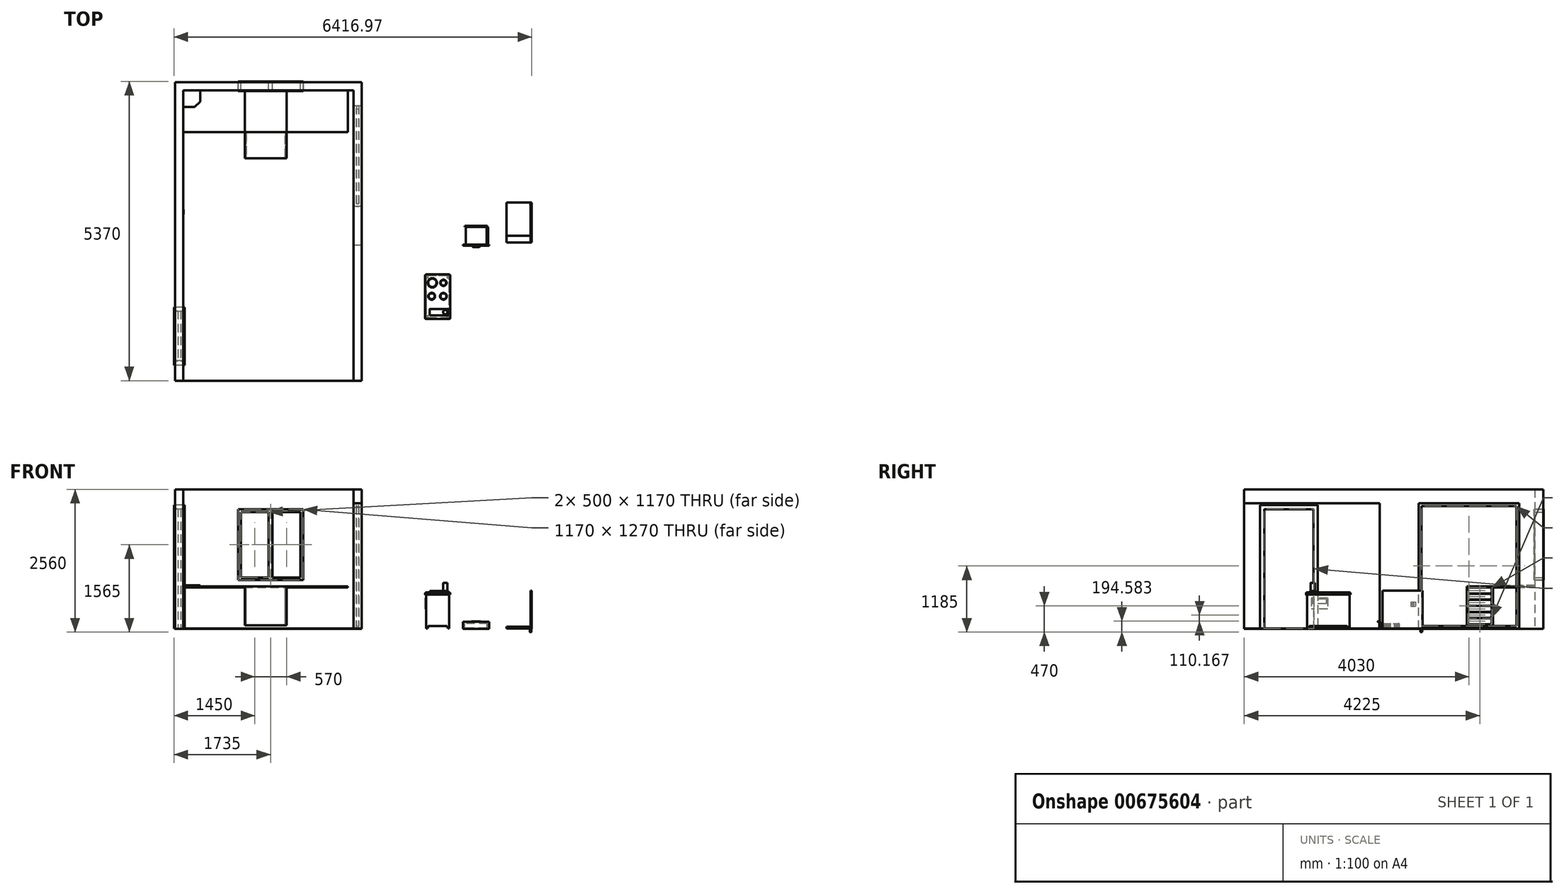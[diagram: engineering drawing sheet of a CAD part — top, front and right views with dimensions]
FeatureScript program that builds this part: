
annotation { "Feature Type Name" : "Feature", "Feature Type Description" : "" }
export const myFeature = defineFeature(function(context is Context, id is Id, definition is map)
    precondition{}
    {
        {
            var Q0;
            Q0=qCreatedBy(makeId("Top.planeOp"),FACE);
            var sketch = newSketch(context, id + "F0", { "sketchPlane" : qUnion([Q0])});
            skLineSegment(sketch, "E0.bottom", {"start": v(-128.32, 3885.41) * mm, "end": v(2921.68, 3885.41) * mm});
            skLineSegment(sketch, "E0.top", {"start": v(-128.32, -74.59) * mm, "end": v(2921.68, -74.59) * mm});
            skLineSegment(sketch, "E0.left", {"start": v(-128.32, 3885.41) * mm, "end": v(-128.32, -74.59) * mm});
            skLineSegment(sketch, "E0.right", {"start": v(2921.68, 3885.41) * mm, "end": v(2921.68, -74.59) * mm});
            skSolve(sketch);
        }
        {
            var Q0;
            Q0=makeQuery(id+"F0.imprint","IMPRINT",FACE,{"disambiguationData":[TD([[makeQuery(id+"F0.imprint","IMPRINT",EDGE,{"derivedFrom":sQuery(id+"F0.wireOp",EDGE,"E0.bottom")}),-1.0]])]});
            var sketch = newSketch(context, id + "F1", { "sketchPlane" : qUnion([Q0])});
            skLineSegment(sketch, "E1.bottom", {"start": v(-278.32, -74.59) * mm, "end": v(-128.32, -74.59) * mm});
            skLineSegment(sketch, "E1.top", {"start": v(-278.32, 4035.41) * mm, "end": v(-128.32, 4035.41) * mm});
            skLineSegment(sketch, "E1.left", {"start": v(-278.32, -74.59) * mm, "end": v(-278.32, 4035.41) * mm});
            skLineSegment(sketch, "E1.right", {"start": v(-128.32, -74.59) * mm, "end": v(-128.32, 3885.41) * mm});
            skLineSegment(sketch, "E2.bottom", {"start": v(-128.32, 4035.41) * mm, "end": v(3071.68, 4035.41) * mm});
            skLineSegment(sketch, "E2.top", {"start": v(-128.32, 3885.41) * mm, "end": v(2921.68, 3885.41) * mm});
            skLineSegment(sketch, "E2.right", {"start": v(3071.68, 4035.41) * mm, "end": v(3071.68, 3885.41) * mm});
            skLineSegment(sketch, "E3.top", {"start": v(3071.68, 3605.41) * mm, "end": v(2921.68, 3605.41) * mm});
            skLineSegment(sketch, "E3.left", {"start": v(3071.68, 3885.41) * mm, "end": v(3071.68, 3605.41) * mm});
            skLineSegment(sketch, "E3.right", {"start": v(2921.68, 3885.41) * mm, "end": v(2921.68, 3605.41) * mm});
            skSolve(sketch);
        }
        {
            var Q0;
            Q0 = qSketchRegion(id + "F1", true);
            extrude(context, id + "F2", {"entities" : qUnion([Q0]), "depth" : 2500 * mm, "offsetDistance" : 25 * mm});
        }
        {
            var Q0;
            Q0=makeQuery(id+"F2.opExtrude","CAP_FACE",FACE,{"disambiguationData":[OSD([sQuery(id+"F1.wireOp",EDGE,"E1.bottom"),sQuery(id+"F1.wireOp",EDGE,"E1.top"),sQuery(id+"F1.wireOp",EDGE,"E1.left"),sQuery(id+"F1.wireOp",EDGE,"E1.right"),sQuery(id+"F1.wireOp",EDGE,"E2.bottom"),sQuery(id+"F1.wireOp",EDGE,"E2.top"),sQuery(id+"F1.wireOp",EDGE,"E2.right"),sQuery(id+"F1.wireOp",EDGE,"E3.top"),sQuery(id+"F1.wireOp",EDGE,"E3.left"),sQuery(id+"F1.wireOp",EDGE,"E3.right")])],"isStart":true});
            var sketch = newSketch(context, id + "F3", { "sketchPlane" : qUnion([Q0])});
            skLineSegment(sketch, "E4.bottom", {"start": v(-278.32, -4035.41) * mm, "end": v(3071.68, -4035.41) * mm});
            skLineSegment(sketch, "E4.top", {"start": v(-278.32, 1324.59) * mm, "end": v(3071.68, 1324.59) * mm});
            skLineSegment(sketch, "E4.left", {"start": v(-278.32, -4035.41) * mm, "end": v(-278.32, 1324.59) * mm});
            skLineSegment(sketch, "E4.right", {"start": v(3071.68, -4035.41) * mm, "end": v(3071.68, 1324.59) * mm});
            skSolve(sketch);
        }
        {
            var Q0;
            Q0 = qSketchRegion(id + "F3", true);
            extrude(context, id + "F4", {"entities" : qUnion([Q0]), "depth" : 5 * mm, "offsetDistance" : 25 * mm});
        }
        {
            var Q0;
            Q0=makeQuery(id+"F2.opExtrude","SWEPT_FACE",FACE,{"disambiguationData":[OSD([sQuery(id+"F1.wireOp",EDGE,"E1.left")])]});
            var sketch = newSketch(context, id + "F5", { "sketchPlane" : qUnion([Q0])});
            skLineSegment(sketch, "E5.bottom", {"start": v(74.59, 0) * mm, "end": v(974.59, 0) * mm});
            skLineSegment(sketch, "E5.top", {"start": v(74.59, 2150) * mm, "end": v(974.59, 2150) * mm});
            skLineSegment(sketch, "E5.left", {"start": v(74.59, 0) * mm, "end": v(74.59, 2150) * mm});
            skLineSegment(sketch, "E5.right", {"start": v(974.59, 0) * mm, "end": v(974.59, 2150) * mm});
            skSolve(sketch);
        }
        {
            var Q0;
            Q0 = qSketchRegion(id + "F5", true);
            extrude(context, id + "F6", {"entities" : qUnion([Q0]), "oppositeDirection" : true, "depth" : 100 * mm, "offsetDistance" : 25 * mm, "hasSecondDirection" : true, "secondDirectionOppositeDirection" : true, "secondDirectionDepth" : 50 * mm});
        }
        {
            var Q0;
            Q0=makeQuery(id+"F2.opExtrude","SWEPT_FACE",FACE,{"disambiguationData":[OSD([sQuery(id+"F1.wireOp",EDGE,"E1.left")])]});
            var sketch = newSketch(context, id + "F7", { "sketchPlane" : qUnion([Q0])});
            skLineSegment(sketch, "E6.bottom", {"start": v(74.59, 2150) * mm, "end": v(974.59, 2150) * mm});
            skLineSegment(sketch, "E6.top", {"start": v(74.59, 2500) * mm, "end": v(974.59, 2500) * mm});
            skLineSegment(sketch, "E6.left", {"start": v(74.59, 2150) * mm, "end": v(74.59, 2500) * mm});
            skLineSegment(sketch, "E6.right", {"start": v(974.59, 2150) * mm, "end": v(974.59, 2500) * mm});
            skLineSegment(sketch, "E7.bottom", {"start": v(974.59, 2500) * mm, "end": v(1324.59, 2500) * mm});
            skLineSegment(sketch, "E7.top", {"start": v(974.59, 0) * mm, "end": v(1324.59, 0) * mm});
            skLineSegment(sketch, "E7.left", {"start": v(974.59, 2500) * mm, "end": v(974.59, 0) * mm});
            skLineSegment(sketch, "E7.right", {"start": v(1324.59, 2500) * mm, "end": v(1324.59, 0) * mm});
            skSolve(sketch);
        }
        {
            var Q0;
            Q0 = qSketchRegion(id + "F7", true);
            var Q1;
            Q1=makeQuery(id+"F2.opExtrude","SWEPT_FACE",FACE,{"disambiguationData":[OSD([sQuery(id+"F1.wireOp",EDGE,"E1.right")])]});
            extrude(context, id + "F8", {"entities" : qUnion([Q0]), "operationType" : NewBodyOperationType.ADD, "endBound" : BoundingType.UP_TO_SURFACE, "oppositeDirection" : true, "depth" : 25 * mm, "endBoundEntityFace" : qUnion([Q1]), "offsetDistance" : 25 * mm});
        }
        {
            var Q0;
            {var subQ0=sQuery(id+"F1.wireOp",EDGE,"E1.right");Q0=makeQuery(id+"F8.boolean.opBoolean","MERGE",FACE,{"derivedFrom":[makeQuery(id+"F2.opExtrude","SWEPT_FACE",FACE,{"disambiguationData":[OSD([subQ0])]}),makeQuery(id+"F8.opExtrude","CAP_FACE",FACE,{"disambiguationData":[OSD([subQ0])],"isStart":false})]});}
            var sketch = newSketch(context, id + "F9", { "sketchPlane" : qUnion([Q0])});
            skLineSegment(sketch, "E8.bottom", {"start": v(-1044.59, 0) * mm, "end": v(-964.59, 0) * mm});
            skLineSegment(sketch, "E8.top", {"start": v(-1044.59, 2220) * mm, "end": v(-964.59, 2220) * mm});
            skLineSegment(sketch, "E8.left", {"start": v(-1044.59, 0) * mm, "end": v(-1044.59, 2220) * mm});
            skLineSegment(sketch, "E8.right", {"start": v(-964.59, 0) * mm, "end": v(-964.59, 2140) * mm});
            skLineSegment(sketch, "E9.bottom", {"start": v(-964.59, 2220) * mm, "end": v(-84.59, 2220) * mm});
            skLineSegment(sketch, "E9.top", {"start": v(-964.59, 2140) * mm, "end": v(-84.59, 2140) * mm});
            skLineSegment(sketch, "E10.bottom", {"start": v(-84.59, 2220) * mm, "end": v(-4.59, 2220) * mm});
            skLineSegment(sketch, "E10.top", {"start": v(-84.59, 0) * mm, "end": v(-4.59, 0) * mm});
            skLineSegment(sketch, "E10.left", {"start": v(-84.59, 2140) * mm, "end": v(-84.59, 0) * mm});
            skLineSegment(sketch, "E10.right", {"start": v(-4.59, 2220) * mm, "end": v(-4.59, 0) * mm});
            skSolve(sketch);
        }
        {
            var Q0;
            Q0 = qSketchRegion(id + "F9", true);
            extrude(context, id + "F10", {"entities" : qUnion([Q0]), "depth" : 20 * mm, "offsetDistance" : 25 * mm, "hasSecondDirection" : true, "secondDirectionOppositeDirection" : true, "secondDirectionDepth" : 170 * mm});
        }
        {
            var Q0;
            Q0=makeQuery(id+"F2.opExtrude","SWEPT_FACE",FACE,{"disambiguationData":[OSD([sQuery(id+"F1.wireOp",EDGE,"E2.top")])]});
            var sketch = newSketch(context, id + "F11", { "sketchPlane" : qUnion([Q0])});
            skLineSegment(sketch, "E11.bottom", {"start": v(851.68, 870) * mm, "end": v(2021.68, 870) * mm});
            skLineSegment(sketch, "E11.top", {"start": v(851.68, 2140) * mm, "end": v(2021.68, 2140) * mm});
            skLineSegment(sketch, "E11.left", {"start": v(851.68, 870) * mm, "end": v(851.68, 2140) * mm});
            skLineSegment(sketch, "E11.right", {"start": v(2021.68, 870) * mm, "end": v(2021.68, 2140) * mm});
            skSolve(sketch);
        }
        {
            var Q0;
            Q0 = qSketchRegion(id + "F11", true);
            extrude(context, id + "F12", {"entities" : qUnion([Q0]), "operationType" : NewBodyOperationType.REMOVE, "oppositeDirection" : true, "depth" : 150 * mm, "offsetDistance" : 25 * mm});
        }
        {
            var Q0;
            Q0=makeQuery(id+"F2.opExtrude","SWEPT_FACE",FACE,{"disambiguationData":[OSD([sQuery(id+"F1.wireOp",EDGE,"E2.top")])]});
            var sketch = newSketch(context, id + "F13", { "sketchPlane" : qUnion([Q0])});
            skLineSegment(sketch, "E12.bottom", {"start": v(851.68, 2140) * mm, "end": v(2021.68, 2140) * mm});
            skLineSegment(sketch, "E12.top", {"start": v(851.68, 870) * mm, "end": v(2021.68, 870) * mm});
            skLineSegment(sketch, "E12.left", {"start": v(851.68, 2140) * mm, "end": v(851.68, 870) * mm});
            skLineSegment(sketch, "E12.right", {"start": v(2021.68, 2140) * mm, "end": v(2021.68, 870) * mm});
            skLineSegment(sketch, "E13.bottom", {"start": v(901.68, 2090) * mm, "end": v(1401.68, 2090) * mm});
            skLineSegment(sketch, "E13.top", {"start": v(901.68, 920) * mm, "end": v(1401.68, 920) * mm});
            skLineSegment(sketch, "E13.left", {"start": v(901.68, 2090) * mm, "end": v(901.68, 920) * mm});
            skLineSegment(sketch, "E13.right", {"start": v(1401.68, 2090) * mm, "end": v(1401.68, 920) * mm});
            skLineSegment(sketch, "E14.bottom", {"start": v(1471.68, 2090) * mm, "end": v(1971.68, 2090) * mm});
            skLineSegment(sketch, "E14.top", {"start": v(1471.68, 920) * mm, "end": v(1971.68, 920) * mm});
            skLineSegment(sketch, "E14.left", {"start": v(1471.68, 2090) * mm, "end": v(1471.68, 920) * mm});
            skLineSegment(sketch, "E14.right", {"start": v(1971.68, 2090) * mm, "end": v(1971.68, 920) * mm});
            skLineSegment(sketch, "E15", {"start": v(1401.68, 2090) * mm, "end": v(1471.68, 2090) * mm, "construction": true});
            skLineSegment(sketch, "E16", {"start": v(1471.68, 920) * mm, "end": v(1401.68, 920) * mm, "construction": true});
            skLineSegment(sketch, "E17", {"start": v(1436.68, 2090) * mm, "end": v(1436.68, 2140) * mm, "construction": true});
            skSolve(sketch);
        }
        {
            var Q0;
            Q0 = qSketchRegion(id + "F13", true);
            extrude(context, id + "F14", {"entities" : qUnion([Q0]), "depth" : 10 * mm, "offsetDistance" : 25 * mm, "hasSecondDirection" : true, "secondDirectionOppositeDirection" : true, "secondDirectionDepth" : 160 * mm});
        }
        {
            var Q0;
            {var subQ0=sQuery(id+"F1.wireOp",EDGE,"E1.right");Q0=makeQuery(id+"F8.boolean.opBoolean","MERGE",FACE,{"derivedFrom":[makeQuery(id+"F2.opExtrude","SWEPT_FACE",FACE,{"disambiguationData":[OSD([subQ0])]}),makeQuery(id+"F8.opExtrude","CAP_FACE",FACE,{"disambiguationData":[OSD([subQ0])],"isStart":false})]});}
            var sketch = newSketch(context, id + "F15", { "sketchPlane" : qUnion([Q0])});
            skLineSegment(sketch, "E18.bottom", {"start": v(1665.41, 480) * mm, "end": v(1745.41, 480) * mm});
            skLineSegment(sketch, "E18.top", {"start": v(1665.41, 400) * mm, "end": v(1745.41, 400) * mm});
            skLineSegment(sketch, "E18.left", {"start": v(1665.41, 480) * mm, "end": v(1665.41, 400) * mm});
            skLineSegment(sketch, "E18.right", {"start": v(1745.41, 480) * mm, "end": v(1745.41, 400) * mm});
            skCircle(sketch, "E19", {"center": v(1705.41, 440) * mm, "radius": 17.85 * mm});
            skPoint(sketch, "E19.centerSnap0", {"position": v(1705.41, 480) * mm});
            skPoint(sketch, "E19.centerSnap1", {"position": v(1745.41, 440) * mm});
            skSolve(sketch);
        }
        {
            var Q0;
            Q0 = qSketchRegion(id + "F15", true);
            extrude(context, id + "F16", {"entities" : qUnion([Q0]), "depth" : 1 * mm, "offsetDistance" : 25 * mm});
        }
        {
            var Q0;
            Q0=makeQuery(id+"F4.opExtrude","CAP_FACE",FACE,{"disambiguationData":[OSD([sQuery(id+"F3.wireOp",EDGE,"E4.bottom"),sQuery(id+"F3.wireOp",EDGE,"E4.top"),sQuery(id+"F3.wireOp",EDGE,"E4.left"),sQuery(id+"F3.wireOp",EDGE,"E4.right")])],"isStart":true});
            var sketch = newSketch(context, id + "F17", { "sketchPlane" : qUnion([Q0])});
            skLineSegment(sketch, "E20.bottom", {"start": v(-128.32, 3885.41) * mm, "end": v(971.68, 3885.41) * mm});
            skLineSegment(sketch, "E20.top", {"start": v(-128.32, 3135.41) * mm, "end": v(971.68, 3135.41) * mm});
            skLineSegment(sketch, "E20.left", {"start": v(-128.32, 3885.41) * mm, "end": v(-128.32, 3135.41) * mm});
            skLineSegment(sketch, "E20.right", {"start": v(971.68, 3885.41) * mm, "end": v(971.68, 3135.41) * mm});
            skSolve(sketch);
        }
        {
            var Q0;
            Q0 = qSketchRegion(id + "F17", true);
            extrude(context, id + "F18", {"entities" : qUnion([Q0]), "depth" : 760 * mm, "offsetDistance" : 25 * mm, "hasSecondDirection" : true, "secondDirectionOppositeDirection" : false, "secondDirectionDepth" : (760 - 18) * mm});
        }
        {
            var Q0;
            Q0=makeQuery(id+"F4.opExtrude","CAP_FACE",FACE,{"disambiguationData":[OSD([sQuery(id+"F3.wireOp",EDGE,"E4.bottom"),sQuery(id+"F3.wireOp",EDGE,"E4.top"),sQuery(id+"F3.wireOp",EDGE,"E4.left"),sQuery(id+"F3.wireOp",EDGE,"E4.right")])],"isStart":true});
            var sketch = newSketch(context, id + "F19", { "sketchPlane" : qUnion([Q0])});
            skLineSegment(sketch, "E21.bottom", {"start": v(971.68, 3885.41) * mm, "end": v(1721.68, 3885.41) * mm});
            skLineSegment(sketch, "E21.top", {"start": v(971.68, 3135.41) * mm, "end": v(1721.68, 3135.41) * mm});
            skLineSegment(sketch, "E21.left", {"start": v(971.68, 3885.41) * mm, "end": v(971.68, 3135.41) * mm});
            skLineSegment(sketch, "E21.right", {"start": v(1721.68, 3885.41) * mm, "end": v(1721.68, 3135.41) * mm});
            skSolve(sketch);
        }
        {
            var Q0;
            Q0 = qSketchRegion(id + "F19", true);
            extrude(context, id + "F20", {"entities" : qUnion([Q0]), "depth" : 760 * mm, "offsetDistance" : 25 * mm, "hasSecondDirection" : true, "secondDirectionOppositeDirection" : false, "secondDirectionDepth" : (760 - 18) * mm});
        }
        {
            var Q0;
            Q0=makeQuery(id+"F4.opExtrude","CAP_FACE",FACE,{"disambiguationData":[OSD([sQuery(id+"F3.wireOp",EDGE,"E4.bottom"),sQuery(id+"F3.wireOp",EDGE,"E4.top"),sQuery(id+"F3.wireOp",EDGE,"E4.left"),sQuery(id+"F3.wireOp",EDGE,"E4.right")])],"isStart":true});
            var sketch = newSketch(context, id + "F21", { "sketchPlane" : qUnion([Q0])});
            skLineSegment(sketch, "E22.bottom", {"start": v(1721.68, 3135.41) * mm, "end": v(2821.68, 3135.41) * mm});
            skLineSegment(sketch, "E22.top", {"start": v(1721.68, 3885.41) * mm, "end": v(2821.68, 3885.41) * mm});
            skLineSegment(sketch, "E22.left", {"start": v(1721.68, 3135.41) * mm, "end": v(1721.68, 3885.41) * mm});
            skLineSegment(sketch, "E22.right", {"start": v(2821.68, 3135.41) * mm, "end": v(2821.68, 3885.41) * mm});
            skSolve(sketch);
        }
        {
            var Q0;
            Q0 = qSketchRegion(id + "F21", true);
            extrude(context, id + "F22", {"entities" : qUnion([Q0]), "depth" : 760 * mm, "offsetDistance" : 25 * mm, "hasSecondDirection" : true, "secondDirectionOppositeDirection" : false, "secondDirectionDepth" : (760 - 18) * mm});
        }
        {
            var Q0;
            Q0=makeQuery(id+"F20.opExtrude","CAP_FACE",FACE,{"disambiguationData":[OSD([sQuery(id+"F19.wireOp",EDGE,"E21.bottom"),sQuery(id+"F19.wireOp",EDGE,"E21.top"),sQuery(id+"F19.wireOp",EDGE,"E21.left"),sQuery(id+"F19.wireOp",EDGE,"E21.right")])],"isStart":false});
            var sketch = newSketch(context, id + "F23", { "sketchPlane" : qUnion([Q0])});
            skLineSegment(sketch, "E23.bottom", {"start": v(971.68, 3135.41) * mm, "end": v(1721.68, 3135.41) * mm});
            skLineSegment(sketch, "E23.top", {"start": v(971.68, 2665.41) * mm, "end": v(1721.68, 2665.41) * mm});
            skLineSegment(sketch, "E23.left", {"start": v(971.68, 3135.41) * mm, "end": v(971.68, 2665.41) * mm});
            skLineSegment(sketch, "E23.right", {"start": v(1721.68, 3135.41) * mm, "end": v(1721.68, 2665.41) * mm});
            skSolve(sketch);
        }
        {
            var Q0;
            Q0 = qSketchRegion(id + "F23", true);
            extrude(context, id + "F24", {"entities" : qUnion([Q0]), "oppositeDirection" : true, "depth" : 700 * mm, "offsetDistance" : 25 * mm});
        }
        {
            var Q0;
            Q0=makeQuery(id+"F24.opExtrude","SWEPT_FACE",FACE,{"disambiguationData":[OSD([sQuery(id+"F23.wireOp",EDGE,"E23.right")])]});
            var sketch = newSketch(context, id + "F25", { "sketchPlane" : qUnion([Q0])});
            skLineSegment(sketch, "E24.0", {"start": v(3117.41, 742) * mm, "end": v(2683.41, 742) * mm});
            skLineSegment(sketch, "E24.1", {"start": v(3117.41, 78) * mm, "end": v(3117.41, 742) * mm});
            skLineSegment(sketch, "E24.2", {"start": v(2683.41, 78) * mm, "end": v(3117.41, 78) * mm});
            skLineSegment(sketch, "E24.3", {"start": v(2683.41, 742) * mm, "end": v(2683.41, 78) * mm});
            skLineSegment(sketch, "E25.0", {"start": v(3113.41, 738) * mm, "end": v(2687.41, 738) * mm});
            skLineSegment(sketch, "E25.1", {"start": v(3113.41, 82) * mm, "end": v(3113.41, 738) * mm});
            skLineSegment(sketch, "E25.2", {"start": v(2687.41, 82) * mm, "end": v(3113.41, 82) * mm});
            skLineSegment(sketch, "E25.3", {"start": v(2687.41, 738) * mm, "end": v(2687.41, 632.83) * mm});
            skLineSegment(sketch, "E26", {"start": v(2687.41, 632.83) * mm, "end": v(3113.41, 632.83) * mm});
            skLineSegment(sketch, "E27", {"start": v(2687.41, 627.83) * mm, "end": v(3113.41, 627.83) * mm});
            skLineSegment(sketch, "E28.0.1.0", {"start": v(2687.41, 522.67) * mm, "end": v(3113.41, 522.67) * mm});
            skLineSegment(sketch, "E28.0.1.1", {"start": v(2687.41, 517.67) * mm, "end": v(3113.41, 517.67) * mm});
            skLineSegment(sketch, "E28.0.2.0", {"start": v(2687.41, 412.5) * mm, "end": v(3113.41, 412.5) * mm});
            skLineSegment(sketch, "E28.0.2.1", {"start": v(2687.41, 407.5) * mm, "end": v(3113.41, 407.5) * mm});
            skLineSegment(sketch, "E28.0.3.0", {"start": v(2687.41, 302.33) * mm, "end": v(3113.41, 302.33) * mm});
            skLineSegment(sketch, "E28.0.3.1", {"start": v(2687.41, 297.33) * mm, "end": v(3113.41, 297.33) * mm});
            skLineSegment(sketch, "E28.0.4.0", {"start": v(2687.41, 192.17) * mm, "end": v(3113.41, 192.17) * mm});
            skLineSegment(sketch, "E28.0.4.1", {"start": v(2687.41, 187.17) * mm, "end": v(3113.41, 187.17) * mm});
            skLineSegment(sketch, "E28.direction1", {"start": v(2032.41, 627.83) * mm, "end": v(2687.41, 627.83) * mm, "construction": true});
            skLineSegment(sketch, "E28.direction2", {"start": v(2687.41, 627.83) * mm, "end": v(2687.41, 522.67) * mm, "construction": true});
            skLineSegment(sketch, "E29", {"start": v(2900.41, 632.83) * mm, "end": v(2900.41, 738) * mm, "construction": true});
            skLineSegment(sketch, "E30", {"start": v(2900.41, 522.67) * mm, "end": v(2900.41, 627.83) * mm, "construction": true});
            skLineSegment(sketch, "E31", {"start": v(2900.41, 82) * mm, "end": v(2900.41, 187.17) * mm, "construction": true});
            skLineSegment(sketch, "E32.trimOffspring", {"start": v(2687.41, 627.83) * mm, "end": v(2687.41, 522.67) * mm});
            skLineSegment(sketch, "E33.trimOffspring", {"start": v(2687.41, 407.5) * mm, "end": v(2687.41, 302.33) * mm});
            skLineSegment(sketch, "E34.trimOffspring", {"start": v(2687.41, 297.33) * mm, "end": v(2687.41, 192.17) * mm});
            skLineSegment(sketch, "E35.trimOffspring", {"start": v(2687.41, 187.17) * mm, "end": v(2687.41, 82) * mm});
            skLineSegment(sketch, "E36.trimOffspring", {"start": v(2687.41, 517.67) * mm, "end": v(2687.41, 412.5) * mm});
            skSolve(sketch);
        }
        {
            var Q0;
            Q0 = qSketchRegion(id + "F25", true);
            extrude(context, id + "F26", {"entities" : qUnion([Q0]), "operationType" : NewBodyOperationType.REMOVE, "oppositeDirection" : true, "depth" : 25 * mm, "offsetDistance" : 25 * mm});
        }
        {
            var Q0;
            Q0=makeQuery(id+"F24.opExtrude","SWEPT_FACE",FACE,{"disambiguationData":[OSD([sQuery(id+"F23.wireOp",EDGE,"E23.left")])]});
            var sketch = newSketch(context, id + "F27", { "sketchPlane" : qUnion([Q0])});
            skLineSegment(sketch, "E37.0", {"start": v(-3117.41, 742) * mm, "end": v(-2683.41, 742) * mm});
            skLineSegment(sketch, "E37.1", {"start": v(-3117.41, 78) * mm, "end": v(-3117.41, 742) * mm});
            skLineSegment(sketch, "E37.2", {"start": v(-2683.41, 78) * mm, "end": v(-3117.41, 78) * mm});
            skLineSegment(sketch, "E37.3", {"start": v(-2683.41, 742) * mm, "end": v(-2683.41, 78) * mm});
            skLineSegment(sketch, "E38.0", {"start": v(-3113.41, 632.83) * mm, "end": v(-3113.41, 738) * mm});
            skLineSegment(sketch, "E38.1", {"start": v(-2687.41, 632.83) * mm, "end": v(-3113.41, 632.83) * mm});
            skLineSegment(sketch, "E38.2", {"start": v(-2687.41, 738) * mm, "end": v(-2687.41, 632.83) * mm});
            skLineSegment(sketch, "E38.3", {"start": v(-3113.41, 738) * mm, "end": v(-2687.41, 738) * mm});
            skLineSegment(sketch, "E39.0", {"start": v(-3113.41, 522.67) * mm, "end": v(-3113.41, 627.83) * mm});
            skLineSegment(sketch, "E39.1", {"start": v(-2687.41, 522.67) * mm, "end": v(-3113.41, 522.67) * mm});
            skLineSegment(sketch, "E39.2", {"start": v(-2687.41, 627.83) * mm, "end": v(-2687.41, 522.67) * mm});
            skLineSegment(sketch, "E39.3", {"start": v(-3113.41, 627.83) * mm, "end": v(-2687.41, 627.83) * mm});
            skLineSegment(sketch, "E40.0", {"start": v(-3113.41, 412.5) * mm, "end": v(-3113.41, 517.67) * mm});
            skLineSegment(sketch, "E40.1", {"start": v(-2687.41, 412.5) * mm, "end": v(-3113.41, 412.5) * mm});
            skLineSegment(sketch, "E40.2", {"start": v(-2687.41, 517.67) * mm, "end": v(-2687.41, 412.5) * mm});
            skLineSegment(sketch, "E40.3", {"start": v(-3113.41, 517.67) * mm, "end": v(-2687.41, 517.67) * mm});
            skLineSegment(sketch, "E41.0", {"start": v(-3113.41, 302.33) * mm, "end": v(-3113.41, 407.5) * mm});
            skLineSegment(sketch, "E41.1", {"start": v(-2687.41, 302.33) * mm, "end": v(-3113.41, 302.33) * mm});
            skLineSegment(sketch, "E41.2", {"start": v(-2687.41, 407.5) * mm, "end": v(-2687.41, 302.33) * mm});
            skLineSegment(sketch, "E41.3", {"start": v(-3113.41, 407.5) * mm, "end": v(-2687.41, 407.5) * mm});
            skLineSegment(sketch, "E42.0", {"start": v(-3113.41, 192.17) * mm, "end": v(-3113.41, 297.33) * mm});
            skLineSegment(sketch, "E42.1", {"start": v(-2687.41, 192.17) * mm, "end": v(-3113.41, 192.17) * mm});
            skLineSegment(sketch, "E42.2", {"start": v(-2687.41, 297.33) * mm, "end": v(-2687.41, 192.17) * mm});
            skLineSegment(sketch, "E42.3", {"start": v(-3113.41, 297.33) * mm, "end": v(-2687.41, 297.33) * mm});
            skLineSegment(sketch, "E43.0", {"start": v(-3113.41, 82) * mm, "end": v(-3113.41, 187.17) * mm});
            skLineSegment(sketch, "E43.1", {"start": v(-2687.41, 82) * mm, "end": v(-3113.41, 82) * mm});
            skLineSegment(sketch, "E43.2", {"start": v(-2687.41, 187.17) * mm, "end": v(-2687.41, 82) * mm});
            skLineSegment(sketch, "E43.3", {"start": v(-3113.41, 187.17) * mm, "end": v(-2687.41, 187.17) * mm});
            skSolve(sketch);
        }
        {
            var Q0;
            Q0 = qSketchRegion(id + "F27", true);
            extrude(context, id + "F28", {"entities" : qUnion([Q0]), "operationType" : NewBodyOperationType.REMOVE, "oppositeDirection" : true, "depth" : 25 * mm, "offsetDistance" : 25 * mm});
        }
        {
            var Q0;
            Q0=makeQuery(id+"F18.opExtrude","CAP_FACE",FACE,{"disambiguationData":[OSD([sQuery(id+"F17.wireOp",EDGE,"E20.bottom"),sQuery(id+"F17.wireOp",EDGE,"E20.top"),sQuery(id+"F17.wireOp",EDGE,"E20.left"),sQuery(id+"F17.wireOp",EDGE,"E20.right")])],"isStart":false});
            var sketch = newSketch(context, id + "F29", { "sketchPlane" : qUnion([Q0])});
            skLineSegment(sketch, "E44.bottom", {"start": v(-128.32, 3885.41) * mm, "end": v(171.68, 3885.41) * mm});
            skLineSegment(sketch, "E44.top", {"start": v(-128.32, 3585.41) * mm, "end": v(71.68, 3585.41) * mm});
            skLineSegment(sketch, "E44.left", {"start": v(-128.32, 3885.41) * mm, "end": v(-128.32, 3585.41) * mm});
            skLineSegment(sketch, "E44.right", {"start": v(171.68, 3885.41) * mm, "end": v(171.68, 3685.41) * mm});
            skLineSegment(sketch, "E45", {"start": v(71.68, 3585.41) * mm, "end": v(171.68, 3685.41) * mm});
            skSolve(sketch);
        }
        {
            var Q0;
            Q0 = qSketchRegion(id + "F29", true);
            extrude(context, id + "F30", {"entities" : qUnion([Q0]), "depth" : 18 * mm, "offsetDistance" : 25 * mm});
        }
        {
            var Q0;
            Q0=qCreatedBy(makeId("Top.planeOp"),FACE);
            var sketch = newSketch(context, id + "F31", { "sketchPlane" : qUnion([Q0])});
            skLineSegment(sketch, "E46.bottom", {"start": v(4887.1, 1493.53) * mm, "end": v(5357.1, 1493.53) * mm, "construction": true});
            skLineSegment(sketch, "E46.top", {"start": v(4887.1, 1118.53) * mm, "end": v(5357.1, 1118.53) * mm, "construction": true});
            skLineSegment(sketch, "E46.left", {"start": v(4887.1, 1493.53) * mm, "end": v(4887.1, 1118.53) * mm, "construction": true});
            skLineSegment(sketch, "E46.right", {"start": v(5357.1, 1493.53) * mm, "end": v(5357.1, 1118.53) * mm, "construction": true});
            skLineSegment(sketch, "E47.bottom", {"start": v(4936.1, 1118.53) * mm, "end": v(5308.1, 1118.53) * mm});
            skLineSegment(sketch, "E47.top", {"start": v(4936.1, 1433.53) * mm, "end": v(5308.1, 1433.53) * mm});
            skLineSegment(sketch, "E47.left", {"start": v(4936.1, 1118.53) * mm, "end": v(4936.1, 1433.53) * mm});
            skLineSegment(sketch, "E47.right", {"start": v(5308.1, 1118.53) * mm, "end": v(5308.1, 1433.53) * mm});
            skSolve(sketch);
        }
        {
            var Q0;
            Q0 = qSketchRegion(id + "F31", true);
            extrude(context, id + "F32", {"entities" : qUnion([Q0]), "depth" : 18 * mm, "offsetDistance" : 25 * mm});
        }
        {
            var Q0;
            Q0=makeQuery(id+"F32.opExtrude","SWEPT_FACE",FACE,{"disambiguationData":[OSD([sQuery(id+"F31.wireOp",EDGE,"E47.right")])]});
            var sketch = newSketch(context, id + "F33", { "sketchPlane" : qUnion([Q0])});
            skLineSegment(sketch, "E48.bottom", {"start": v(1118.53, 0) * mm, "end": v(1433.53, 0) * mm});
            skLineSegment(sketch, "E48.top", {"start": v(1118.53, 90) * mm, "end": v(1433.53, 90) * mm});
            skLineSegment(sketch, "E48.left", {"start": v(1118.53, 0) * mm, "end": v(1118.53, 90) * mm});
            skLineSegment(sketch, "E48.right", {"start": v(1433.53, 0) * mm, "end": v(1433.53, 90) * mm});
            skSolve(sketch);
        }
        {
            var Q0;
            Q0 = qSketchRegion(id + "F33", true);
            extrude(context, id + "F34", {"entities" : qUnion([Q0]), "depth" : 18 * mm, "offsetDistance" : 25 * mm});
        }
        {
            var Q0;
            Q0=makeQuery(id+"F34.opExtrude","SWEPT_FACE",FACE,{"disambiguationData":[OSD([sQuery(id+"F33.wireOp",EDGE,"E48.right")])]});
            var sketch = newSketch(context, id + "F35", { "sketchPlane" : qUnion([Q0])});
            skLineSegment(sketch, "E49.bottom", {"start": v(-5326.1, 0) * mm, "end": v(-4918.1, 0) * mm});
            skLineSegment(sketch, "E49.top", {"start": v(-5326.1, 90) * mm, "end": v(-4918.1, 90) * mm});
            skLineSegment(sketch, "E49.left", {"start": v(-5326.1, 0) * mm, "end": v(-5326.1, 90) * mm});
            skLineSegment(sketch, "E49.right", {"start": v(-4918.1, 0) * mm, "end": v(-4918.1, 90) * mm});
            skSolve(sketch);
        }
        {
            var Q0;
            Q0 = qSketchRegion(id + "F35", true);
            extrude(context, id + "F36", {"entities" : qUnion([Q0]), "depth" : 18 * mm, "offsetDistance" : 25 * mm});
        }
        {
            var Q0;
            Q0=makeQuery(id+"F32.opExtrude","SWEPT_FACE",FACE,{"disambiguationData":[OSD([sQuery(id+"F31.wireOp",EDGE,"E47.bottom")])]});
            var sketch = newSketch(context, id + "F37", { "sketchPlane" : qUnion([Q0])});
            skLineSegment(sketch, "E50.bottom", {"start": v(4887.1, 122) * mm, "end": v(5357.1, 122) * mm});
            skLineSegment(sketch, "E50.top", {"start": v(4887.1, -5) * mm, "end": v(5357.1, -5) * mm});
            skLineSegment(sketch, "E50.left", {"start": v(4887.1, 122) * mm, "end": v(4887.1, -5) * mm});
            skLineSegment(sketch, "E50.right", {"start": v(5357.1, 122) * mm, "end": v(5357.1, -5) * mm});
            skLineSegment(sketch, "E51", {"start": v(5122.1, 122) * mm, "end": v(5122.1, 90) * mm, "construction": true});
            skSolve(sketch);
        }
        {
            var Q0;
            Q0 = qSketchRegion(id + "F37", true);
            extrude(context, id + "F38", {"entities" : qUnion([Q0]), "depth" : 18 * mm, "offsetDistance" : 25 * mm});
        }
        {
            var Q0;
            Q0=makeQuery(id+"F34.opExtrude","CAP_FACE",FACE,{"disambiguationData":[OSD([sQuery(id+"F33.wireOp",EDGE,"E48.bottom"),sQuery(id+"F33.wireOp",EDGE,"E48.top"),sQuery(id+"F33.wireOp",EDGE,"E48.left"),sQuery(id+"F33.wireOp",EDGE,"E48.right")])],"isStart":false});
            var sketch = newSketch(context, id + "F39", { "sketchPlane" : qUnion([Q0])});
            skLineSegment(sketch, "E52.bottom", {"start": v(1126.15, 71.9) * mm, "end": v(1426.15, 71.9) * mm});
            skLineSegment(sketch, "E52.top", {"start": v(1126.15, 35.9) * mm, "end": v(1426.15, 35.9) * mm});
            skLineSegment(sketch, "E52.left", {"start": v(1126.15, 71.9) * mm, "end": v(1126.15, 35.9) * mm});
            skLineSegment(sketch, "E52.right", {"start": v(1426.15, 71.9) * mm, "end": v(1426.15, 35.9) * mm});
            skSolve(sketch);
        }
        {
            var Q0;
            Q0 = qSketchRegion(id + "F39", true);
            extrude(context, id + "F40", {"entities" : qUnion([Q0]), "depth" : 13 * mm, "offsetDistance" : 25 * mm});
        }
        {
            var Q0;
            Q0=makeQuery(id+"F38.opExtrude","SWEPT_FACE",FACE,{"disambiguationData":[OSD([sQuery(id+"F37.wireOp",EDGE,"E50.bottom")])]});
            var sketch = newSketch(context, id + "F41", { "sketchPlane" : qUnion([Q0])});
            skLineSegment(sketch, "E53", {"start": v(5042.1, 1100.53) * mm, "end": v(5069.35, 1070.53) * mm});
            skLineSegment(sketch, "E54", {"start": v(5069.35, 1070.53) * mm, "end": v(5174.86, 1070.53) * mm});
            skLineSegment(sketch, "E55", {"start": v(5174.86, 1070.53) * mm, "end": v(5202.1, 1100.53) * mm});
            skLineSegment(sketch, "E56", {"start": v(5122.1, 1070.53) * mm, "end": v(5122.1, 1100.53) * mm, "construction": true});
            skLineSegment(sketch, "E57", {"start": v(5042.1, 1100.53) * mm, "end": v(5202.1, 1100.53) * mm, "construction": true});
            skLineSegment(sketch, "E58.0", {"start": v(5171.76, 1077.53) * mm, "end": v(5192.65, 1100.53) * mm});
            skLineSegment(sketch, "E58.1", {"start": v(5072.45, 1077.53) * mm, "end": v(5171.76, 1077.53) * mm});
            skLineSegment(sketch, "E58.2", {"start": v(5051.56, 1100.53) * mm, "end": v(5072.45, 1077.53) * mm});
            skLineSegment(sketch, "E59", {"start": v(5042.1, 1100.53) * mm, "end": v(5051.56, 1100.53) * mm});
            skLineSegment(sketch, "E60", {"start": v(5192.65, 1100.53) * mm, "end": v(5202.1, 1100.53) * mm});
            skSolve(sketch);
        }
        {
            var Q0;
            Q0 = qSketchRegion(id + "F41", true);
            extrude(context, id + "F42", {"entities" : qUnion([Q0]), "depth" : 9 * mm, "offsetDistance" : 25 * mm});
        }
        {
            var Q0;
            Q0=makeQuery(id+"F42.opExtrude","SWEPT_EDGE",EDGE,{"disambiguationData":[OSD([sQuery(id+"F41.wireOp",EDGE,"E53"),sQuery(id+"F41.wireOp",EDGE,"E54")])]});
            var Q1;
            Q1=makeQuery(id+"F42.opExtrude","SWEPT_EDGE",EDGE,{"disambiguationData":[OSD([sQuery(id+"F41.wireOp",EDGE,"E54"),sQuery(id+"F41.wireOp",EDGE,"E55")])]});
            var Q2;
            Q2=makeQuery(id+"F42.opExtrude","SWEPT_EDGE",EDGE,{"disambiguationData":[OSD([sQuery(id+"F41.wireOp",EDGE,"E58.1"),sQuery(id+"F41.wireOp",EDGE,"E58.2")])]});
            var Q3;
            Q3=makeQuery(id+"F42.opExtrude","SWEPT_EDGE",EDGE,{"disambiguationData":[OSD([sQuery(id+"F41.wireOp",EDGE,"E58.0"),sQuery(id+"F41.wireOp",EDGE,"E58.1")])]});
            fillet(context, id + "F43", {"entities" : qUnion([Q0, Q1, Q2, Q3]), "radius" : 25 * mm, "tangentPropagation" : true, "allowEdgeOverflow" : false});
        }
        {
            var Q0;
            Q0=makeQuery(id+"F42.opExtrude","CAP_EDGE",EDGE,{"disambiguationData":[OSD([sQuery(id+"F41.wireOp",EDGE,"E53")])],"isStart":false});
            var Q1;
            Q1=makeQuery(id+"F42.opExtrude","CAP_EDGE",EDGE,{"disambiguationData":[OSD([sQuery(id+"F41.wireOp",EDGE,"E54")])],"isStart":false});
            var Q2;
            Q2=makeQuery(id+"F42.opExtrude","CAP_EDGE",EDGE,{"disambiguationData":[OSD([sQuery(id+"F41.wireOp",EDGE,"E54")])],"isStart":true});
            var Q3;
            Q3=makeQuery(id+"F42.opExtrude","CAP_EDGE",EDGE,{"disambiguationData":[OSD([sQuery(id+"F41.wireOp",EDGE,"E53")])],"isStart":true});
            var Q4;
            Q4=makeQuery(id+"F42.opExtrude","CAP_EDGE",EDGE,{"disambiguationData":[OSD([sQuery(id+"F41.wireOp",EDGE,"E55")])],"isStart":false});
            var Q5;
            Q5=makeQuery(id+"F42.opExtrude","CAP_EDGE",EDGE,{"disambiguationData":[OSD([sQuery(id+"F41.wireOp",EDGE,"E55")])],"isStart":true});
            var Q6;
            Q6=makeQuery(id+"F42.opExtrude","CAP_EDGE",EDGE,{"disambiguationData":[OSD([sQuery(id+"F41.wireOp",EDGE,"E58.0")])],"isStart":false});
            var Q7;
            Q7=makeQuery(id+"F42.opExtrude","CAP_EDGE",EDGE,{"disambiguationData":[OSD([sQuery(id+"F41.wireOp",EDGE,"E58.1")])],"isStart":false});
            var Q8;
            Q8=makeQuery(id+"F42.opExtrude","CAP_EDGE",EDGE,{"disambiguationData":[OSD([sQuery(id+"F41.wireOp",EDGE,"E58.2")])],"isStart":false});
            var Q9;
            Q9=makeQuery(id+"F42.opExtrude","CAP_EDGE",EDGE,{"disambiguationData":[OSD([sQuery(id+"F41.wireOp",EDGE,"E58.2")])],"isStart":true});
            var Q10;
            Q10=makeQuery(id+"F42.opExtrude","CAP_EDGE",EDGE,{"disambiguationData":[OSD([sQuery(id+"F41.wireOp",EDGE,"E58.1")])],"isStart":true});
            var Q11;
            Q11=makeQuery(id+"F42.opExtrude","CAP_EDGE",EDGE,{"disambiguationData":[OSD([sQuery(id+"F41.wireOp",EDGE,"E58.0")])],"isStart":true});
            fillet(context, id + "F44", {"entities" : qUnion([Q0, Q1, Q2, Q3, Q4, Q5, Q6, Q7, Q8, Q9, Q10, Q11]), "radius" : 1 * mm, "tangentPropagation" : true, "allowEdgeOverflow" : false});
        }
        {
            var Q0;
            Q0=qCreatedBy(makeId("Top.planeOp"),FACE);
            var sketch = newSketch(context, id + "F45", { "sketchPlane" : qUnion([Q0])});
            skLineSegment(sketch, "E61.bottom", {"start": v(5666.65, 1157.68) * mm, "end": v(6100.65, 1157.68) * mm});
            skLineSegment(sketch, "E61.top", {"start": v(5666.65, 1871.68) * mm, "end": v(6100.65, 1871.68) * mm});
            skLineSegment(sketch, "E61.left", {"start": v(5666.65, 1157.68) * mm, "end": v(5666.65, 1871.68) * mm});
            skLineSegment(sketch, "E61.right", {"start": v(6100.65, 1157.68) * mm, "end": v(6100.65, 1871.68) * mm});
            skSolve(sketch);
        }
        {
            var Q0;
            Q0 = qSketchRegion(id + "F45", true);
            extrude(context, id + "F46", {"entities" : qUnion([Q0]), "depth" : 18 * mm, "offsetDistance" : 25 * mm});
        }
        {
            var Q0;
            Q0=makeQuery(id+"F46.opExtrude","SWEPT_FACE",FACE,{"disambiguationData":[OSD([sQuery(id+"F45.wireOp",EDGE,"E61.right")])]});
            var sketch = newSketch(context, id + "F47", { "sketchPlane" : qUnion([Q0])});
            skLineSegment(sketch, "E62.bottom", {"start": v(1157.68, 0) * mm, "end": v(1871.68, 0) * mm});
            skLineSegment(sketch, "E62.top", {"start": v(1157.68, 682) * mm, "end": v(1871.68, 682) * mm});
            skLineSegment(sketch, "E62.left", {"start": v(1157.68, 0) * mm, "end": v(1157.68, 682) * mm});
            skLineSegment(sketch, "E62.right", {"start": v(1871.68, 0) * mm, "end": v(1871.68, 682) * mm});
            skSolve(sketch);
        }
        {
            var Q0;
            Q0 = qSketchRegion(id + "F47", true);
            extrude(context, id + "F48", {"entities" : qUnion([Q0]), "depth" : 18 * mm, "offsetDistance" : 25 * mm});
        }
        {
            var Q0;
            Q0=makeQuery(id+"F46.opExtrude","CAP_FACE",FACE,{"disambiguationData":[OSD([sQuery(id+"F45.wireOp",EDGE,"E61.bottom"),sQuery(id+"F45.wireOp",EDGE,"E61.top"),sQuery(id+"F45.wireOp",EDGE,"E61.left"),sQuery(id+"F45.wireOp",EDGE,"E61.right")])],"isStart":false});
            var sketch = newSketch(context, id + "F49", { "sketchPlane" : qUnion([Q0])});
            skLineSegment(sketch, "E63.bottom", {"start": v(5666.65, 1157.68) * mm, "end": v(6100.65, 1157.68) * mm});
            skLineSegment(sketch, "E63.top", {"start": v(5666.65, 1277.68) * mm, "end": v(6100.65, 1277.68) * mm});
            skLineSegment(sketch, "E63.left", {"start": v(5666.65, 1157.68) * mm, "end": v(5666.65, 1277.68) * mm});
            skLineSegment(sketch, "E63.right", {"start": v(6100.65, 1157.68) * mm, "end": v(6100.65, 1277.68) * mm});
            skSolve(sketch);
        }
        {
            var Q0;
            Q0 = qSketchRegion(id + "F49", true);
            extrude(context, id + "F50", {"entities" : qUnion([Q0]), "depth" : 18 * mm, "offsetDistance" : 25 * mm});
        }
        {
            var Q0;
            Q0=makeQuery(id+"F46.opExtrude","CAP_FACE",FACE,{"disambiguationData":[OSD([sQuery(id+"F45.wireOp",EDGE,"E61.bottom"),sQuery(id+"F45.wireOp",EDGE,"E61.top"),sQuery(id+"F45.wireOp",EDGE,"E61.left"),sQuery(id+"F45.wireOp",EDGE,"E61.right")])],"isStart":true});
            var sketch = newSketch(context, id + "F51", { "sketchPlane" : qUnion([Q0])});
            skLineSegment(sketch, "E64.bottom", {"start": v(6118.65, -1871.68) * mm, "end": v(6076.65, -1871.68) * mm});
            skLineSegment(sketch, "E64.top", {"start": v(6118.65, -1829.68) * mm, "end": v(6076.65, -1829.68) * mm});
            skLineSegment(sketch, "E64.left", {"start": v(6118.65, -1871.68) * mm, "end": v(6118.65, -1829.68) * mm});
            skLineSegment(sketch, "E64.right", {"start": v(6076.65, -1871.68) * mm, "end": v(6076.65, -1829.68) * mm});
            skPoint(sketch, "E65.centerSnap0", {"position": v(6076.65, -1850.68) * mm});
            skPoint(sketch, "E65.centerSnap1", {"position": v(6097.65, -1829.68) * mm});
            skSolve(sketch);
        }
        {
            var Q0;
            Q0 = qSketchRegion(id + "F51", true);
            extrude(context, id + "F52", {"entities" : qUnion([Q0]), "depth" : 2 * mm, "offsetDistance" : 25 * mm});
        }
        {
            var Q0;
            Q0=makeQuery(id+"F52.opExtrude","CAP_FACE",FACE,{"disambiguationData":[OSD([sQuery(id+"F51.wireOp",EDGE,"E64.bottom"),sQuery(id+"F51.wireOp",EDGE,"E64.top"),sQuery(id+"F51.wireOp",EDGE,"E64.left"),sQuery(id+"F51.wireOp",EDGE,"E64.right")])],"isStart":false});
            var sketch = newSketch(context, id + "F53", { "sketchPlane" : qUnion([Q0])});
            skCircle(sketch, "E66", {"center": v(6097.65, -1850.68) * mm, "radius": 15 * mm});
            skPoint(sketch, "E66.centerSnap0", {"position": v(6076.65, -1850.68) * mm});
            skPoint(sketch, "E66.centerSnap1", {"position": v(6097.65, -1829.68) * mm});
            skSolve(sketch);
        }
        {
            var Q0;
            Q0 = qSketchRegion(id + "F53", true);
            extrude(context, id + "F54", {"entities" : qUnion([Q0]), "operationType" : NewBodyOperationType.ADD, "depth" : 58 * mm, "offsetDistance" : 25 * mm});
        }
        {
            var Q0;
            Q0=makeQuery(id+"F54.opExtrude","CAP_EDGE",EDGE,{"disambiguationData":[OSD([sQuery(id+"F53.wireOp",EDGE,"E66")])],"isStart":false});
            fillet(context, id + "F55", {"entities" : qUnion([Q0]), "radius" : 3 * mm, "tangentPropagation" : true, "allowEdgeOverflow" : false});
        }
        {
            var Q0;
            Q0=makeQuery(id+"F40.opExtrude","CAP_FACE",FACE,{"disambiguationData":[OSD([sQuery(id+"F39.wireOp",EDGE,"E52.bottom"),sQuery(id+"F39.wireOp",EDGE,"E52.top"),sQuery(id+"F39.wireOp",EDGE,"E52.left"),sQuery(id+"F39.wireOp",EDGE,"E52.right")])],"isStart":false});
            var sketch = newSketch(context, id + "F56", { "sketchPlane" : qUnion([Q0])});
            skLineSegment(sketch, "E67.bottom", {"start": v(1126.15, 68.9) * mm, "end": v(1426.15, 68.9) * mm});
            skLineSegment(sketch, "E67.top", {"start": v(1126.15, 38.9) * mm, "end": v(1426.15, 38.9) * mm});
            skLineSegment(sketch, "E67.left", {"start": v(1126.15, 68.9) * mm, "end": v(1126.15, 38.9) * mm});
            skLineSegment(sketch, "E67.right", {"start": v(1426.15, 68.9) * mm, "end": v(1426.15, 38.9) * mm});
            skSolve(sketch);
        }
        {
            var Q0;
            Q0 = qSketchRegion(id + "F56", true);
            extrude(context, id + "F57", {"entities" : qUnion([Q0]), "operationType" : NewBodyOperationType.REMOVE, "oppositeDirection" : true, "depth" : 10 * mm, "offsetDistance" : 25 * mm});
        }
        {
            var Q0;
            Q0=makeQuery(id+"F57.boolean.opBoolean","COPY",EDGE,{"derivedFrom":makeQuery(id+"F57.opExtrude","CAP_EDGE",EDGE,{"disambiguationData":[OSD([sQuery(id+"F56.wireOp",EDGE,"E67.top")])],"isStart":false})});
            var Q1;
            Q1=makeQuery(id+"F57.boolean.opBoolean","COPY",EDGE,{"derivedFrom":makeQuery(id+"F57.opExtrude","CAP_EDGE",EDGE,{"disambiguationData":[OSD([sQuery(id+"F56.wireOp",EDGE,"E67.bottom")])],"isStart":false})});
            var Q2;
            Q2=makeQuery(id+"F40.opExtrude","CAP_EDGE",EDGE,{"disambiguationData":[OSD([sQuery(id+"F39.wireOp",EDGE,"E52.top")])],"isStart":true});
            var Q3;
            Q3=makeQuery(id+"F40.opExtrude","CAP_EDGE",EDGE,{"disambiguationData":[OSD([sQuery(id+"F39.wireOp",EDGE,"E52.bottom")])],"isStart":true});
            fillet(context, id + "F58", {"entities" : qUnion([Q0, Q1, Q2, Q3]), "radius" : 5 * mm, "tangentPropagation" : true, "allowEdgeOverflow" : false});
        }
        {
            var Q0;
            Q0=qCreatedBy(makeId("Top.planeOp"),FACE);
            var sketch = newSketch(context, id + "F59", { "sketchPlane" : qUnion([Q0])});
            skLineSegment(sketch, "E68.bottom", {"start": v(4207.63, 581.6) * mm, "end": v(4657.63, 581.6) * mm});
            skLineSegment(sketch, "E68.top", {"start": v(4207.63, -218.4) * mm, "end": v(4657.63, -218.4) * mm});
            skLineSegment(sketch, "E68.left", {"start": v(4207.63, 581.6) * mm, "end": v(4207.63, -218.4) * mm});
            skLineSegment(sketch, "E68.right", {"start": v(4657.63, 581.6) * mm, "end": v(4657.63, -218.4) * mm});
            skSolve(sketch);
        }
        {
            var Q0;
            Q0 = qSketchRegion(id + "F59", true);
            extrude(context, id + "F60", {"entities" : qUnion([Q0]), "depth" : 650 * mm, "offsetDistance" : 25 * mm});
        }
        {
            var Q0;
            Q0=makeQuery(id+"F60.opExtrude","SWEPT_FACE",FACE,{"disambiguationData":[OSD([sQuery(id+"F59.wireOp",EDGE,"E68.right")])]});
            var sketch = newSketch(context, id + "F61", { "sketchPlane" : qUnion([Q0])});
            skLineSegment(sketch, "E69.bottom", {"start": v(-218.4, 611.09) * mm, "end": v(581.6, 611.09) * mm});
            skLineSegment(sketch, "E69.top", {"start": v(-218.4, 0) * mm, "end": v(581.6, 0) * mm});
            skLineSegment(sketch, "E69.left", {"start": v(-218.4, 611.09) * mm, "end": v(-218.4, 0) * mm});
            skLineSegment(sketch, "E69.right", {"start": v(581.6, 611.09) * mm, "end": v(581.6, 0) * mm});
            skSolve(sketch);
        }
        {
            var Q0;
            Q0 = qSketchRegion(id + "F61", true);
            extrude(context, id + "F62", {"entities" : qUnion([Q0]), "operationType" : NewBodyOperationType.REMOVE, "oppositeDirection" : true, "depth" : 20 * mm, "offsetDistance" : 25 * mm});
        }
        {
            var Q0;
            Q0=makeQuery(id+"F60.opExtrude","SWEPT_FACE",FACE,{"disambiguationData":[OSD([sQuery(id+"F59.wireOp",EDGE,"E68.top")])]});
            var sketch = newSketch(context, id + "F63", { "sketchPlane" : qUnion([Q0])});
            skLineSegment(sketch, "E70.bottom", {"start": v(4637.63, 611.09) * mm, "end": v(4207.63, 611.09) * mm});
            skLineSegment(sketch, "E70.top", {"start": v(4637.63, 0) * mm, "end": v(4207.63, 0) * mm});
            skLineSegment(sketch, "E70.left", {"start": v(4637.63, 611.09) * mm, "end": v(4637.63, 0) * mm});
            skLineSegment(sketch, "E70.right", {"start": v(4207.63, 611.09) * mm, "end": v(4207.63, 0) * mm});
            skSolve(sketch);
        }
        {
            var Q0;
            Q0 = qSketchRegion(id + "F63", true);
            extrude(context, id + "F64", {"entities" : qUnion([Q0]), "operationType" : NewBodyOperationType.REMOVE, "oppositeDirection" : true, "depth" : 20 * mm, "offsetDistance" : 25 * mm});
        }
        {
            var Q0;
            Q0=makeQuery(id+"F60.opExtrude","SWEPT_FACE",FACE,{"disambiguationData":[OSD([sQuery(id+"F59.wireOp",EDGE,"E68.left")])]});
            var sketch = newSketch(context, id + "F65", { "sketchPlane" : qUnion([Q0])});
            skLineSegment(sketch, "E71.bottom", {"start": v(198.4, 611.09) * mm, "end": v(-581.6, 611.09) * mm});
            skLineSegment(sketch, "E71.top", {"start": v(198.4, -14.4) * mm, "end": v(-581.6, -14.4) * mm});
            skLineSegment(sketch, "E71.left", {"start": v(198.4, 611.09) * mm, "end": v(198.4, -14.4) * mm});
            skLineSegment(sketch, "E71.right", {"start": v(-581.6, 611.09) * mm, "end": v(-581.6, -14.4) * mm});
            skSolve(sketch);
        }
        {
            var Q0;
            Q0 = qSketchRegion(id + "F65", true);
            extrude(context, id + "F66", {"entities" : qUnion([Q0]), "operationType" : NewBodyOperationType.REMOVE, "oppositeDirection" : true, "depth" : 20 * mm, "offsetDistance" : 25 * mm});
        }
        {
            var Q0;
            Q0=makeQuery(id+"F60.opExtrude","SWEPT_FACE",FACE,{"disambiguationData":[OSD([sQuery(id+"F59.wireOp",EDGE,"E68.bottom")])]});
            var sketch = newSketch(context, id + "F67", { "sketchPlane" : qUnion([Q0])});
            skLineSegment(sketch, "E72.bottom", {"start": v(-4637.63, 611.09) * mm, "end": v(-4227.63, 611.09) * mm});
            skLineSegment(sketch, "E72.top", {"start": v(-4637.63, 0) * mm, "end": v(-4227.63, 0) * mm});
            skLineSegment(sketch, "E72.left", {"start": v(-4637.63, 611.09) * mm, "end": v(-4637.63, 0) * mm});
            skLineSegment(sketch, "E72.right", {"start": v(-4227.63, 611.09) * mm, "end": v(-4227.63, 0) * mm});
            skSolve(sketch);
        }
        {
            var Q0;
            Q0 = qSketchRegion(id + "F67", true);
            extrude(context, id + "F68", {"entities" : qUnion([Q0]), "operationType" : NewBodyOperationType.REMOVE, "oppositeDirection" : true, "depth" : 20 * mm, "offsetDistance" : 25 * mm});
        }
        {
            var Q0;
            Q0=makeQuery(id+"F60.opExtrude","CAP_FACE",FACE,{"disambiguationData":[OSD([sQuery(id+"F59.wireOp",EDGE,"E68.bottom"),sQuery(id+"F59.wireOp",EDGE,"E68.top"),sQuery(id+"F59.wireOp",EDGE,"E68.left"),sQuery(id+"F59.wireOp",EDGE,"E68.right")])],"isStart":false});
            var Q1;
            Q1=makeQuery(id+"F60.opExtrude","SWEPT_EDGE",EDGE,{"disambiguationData":[OSD([sQuery(id+"F59.wireOp",EDGE,"E68.top"),sQuery(id+"F59.wireOp",EDGE,"E68.right")])]});
            var Q2;
            Q2=makeQuery(id+"F60.opExtrude","SWEPT_EDGE",EDGE,{"disambiguationData":[OSD([sQuery(id+"F59.wireOp",EDGE,"E68.top"),sQuery(id+"F59.wireOp",EDGE,"E68.left")])]});
            var Q3;
            Q3=makeQuery(id+"F60.opExtrude","SWEPT_EDGE",EDGE,{"disambiguationData":[OSD([sQuery(id+"F59.wireOp",EDGE,"E68.bottom"),sQuery(id+"F59.wireOp",EDGE,"E68.left")])]});
            var Q4;
            Q4=makeQuery(id+"F60.opExtrude","SWEPT_EDGE",EDGE,{"disambiguationData":[OSD([sQuery(id+"F59.wireOp",EDGE,"E68.bottom"),sQuery(id+"F59.wireOp",EDGE,"E68.right")])]});
            var Q5;
            Q5=makeQuery(id+"F68.boolean.opBoolean","COPY",EDGE,{"derivedFrom":makeQuery(id+"F68.opExtrude","CAP_EDGE",EDGE,{"disambiguationData":[OSD([sQuery(id+"F67.wireOp",EDGE,"E72.left")])],"isStart":false})});
            var Q6;
            Q6=makeQuery(id+"F68.boolean.opBoolean","COPY",EDGE,{"derivedFrom":makeQuery(id+"F68.opExtrude","CAP_EDGE",EDGE,{"disambiguationData":[OSD([sQuery(id+"F67.wireOp",EDGE,"E72.right")])],"isStart":false})});
            var Q7;
            Q7=makeQuery(id+"F66.boolean.opBoolean","COPY",EDGE,{"derivedFrom":makeQuery(id+"F66.opExtrude","CAP_EDGE",EDGE,{"disambiguationData":[OSD([sQuery(id+"F65.wireOp",EDGE,"E71.left")])],"isStart":false})});
            var Q8;
            Q8=makeQuery(id+"F64.boolean.opBoolean","COPY",EDGE,{"derivedFrom":makeQuery(id+"F64.opExtrude","CAP_EDGE",EDGE,{"disambiguationData":[OSD([sQuery(id+"F63.wireOp",EDGE,"E70.left")])],"isStart":false})});
            fillet(context, id + "F69", {"entities" : qUnion([Q0, Q1, Q2, Q3, Q4, Q5, Q6, Q7, Q8]), "radius" : 20 * mm, "tangentPropagation" : true, "allowEdgeOverflow" : false});
        }
        {
            var Q0;
            Q0=makeQuery(id+"F60.opExtrude","CAP_FACE",FACE,{"disambiguationData":[OSD([sQuery(id+"F59.wireOp",EDGE,"E68.bottom"),sQuery(id+"F59.wireOp",EDGE,"E68.top"),sQuery(id+"F59.wireOp",EDGE,"E68.left"),sQuery(id+"F59.wireOp",EDGE,"E68.right")])],"isStart":false});
            var sketch = newSketch(context, id + "F70", { "sketchPlane" : qUnion([Q0])});
            skCircle(sketch, "E73", {"center": v(4336.22, 432.37) * mm, "radius": 83.47 * mm});
            skCircle(sketch, "E74", {"center": v(4336.22, 432.37) * mm, "radius": 74.16 * mm});
            skCircle(sketch, "E75", {"center": v(4535.5, 432.37) * mm, "radius": 48.16 * mm});
            skCircle(sketch, "E76", {"center": v(4535.5, 432.37) * mm, "radius": 56.73 * mm});
            skCircle(sketch, "E77", {"center": v(4325.2, 191.03) * mm, "radius": 62 * mm});
            skCircle(sketch, "E78", {"center": v(4325.2, 191.03) * mm, "radius": 53.41 * mm});
            skCircle(sketch, "E79", {"center": v(4535.5, 191.03) * mm, "radius": 52.85 * mm});
            skCircle(sketch, "E80", {"center": v(4535.5, 191.03) * mm, "radius": 61.22 * mm});
            skSolve(sketch);
        }
        {
            var Q0;
            Q0 = qSketchRegion(id + "F70", true);
            extrude(context, id + "F71", {"entities" : qUnion([Q0]), "operationType" : NewBodyOperationType.REMOVE, "oppositeDirection" : true, "depth" : 3 * mm, "offsetDistance" : 25 * mm});
        }
        {
            var Q0;
            {var subQ0=sQuery(id+"F59.wireOp",EDGE,"E68.right");var subQ1=sQuery(id+"F59.wireOp",EDGE,"E68.left");var subQ2=sQuery(id+"F59.wireOp",EDGE,"E68.top");var subQ3=sQuery(id+"F59.wireOp",EDGE,"E68.bottom");Q0=makeQuery(id+"F71.boolean.opBoolean","SPLIT",FACE,{"disambiguationData":[TD([makeQuery(id+"F69.opFillet","BLEND_FACE",FACE,{"disambiguationData":[OSD([subQ3])]})])],"derivedFrom":makeQuery(id+"F60.opExtrude","CAP_FACE",FACE,{"disambiguationData":[OSD([subQ3,subQ2,subQ1,subQ0])],"isStart":false})});}
            var sketch = newSketch(context, id + "F72", { "sketchPlane" : qUnion([Q0])});
            skLineSegment(sketch, "E81.bottom", {"start": v(4287.86, -35.02) * mm, "end": v(4625.09, -35.02) * mm});
            skLineSegment(sketch, "E81.top", {"start": v(4287.86, -149.18) * mm, "end": v(4625.09, -149.18) * mm});
            skLineSegment(sketch, "E81.left", {"start": v(4287.86, -35.02) * mm, "end": v(4287.86, -149.18) * mm});
            skLineSegment(sketch, "E81.right", {"start": v(4625.09, -35.02) * mm, "end": v(4625.09, -149.18) * mm});
            skSolve(sketch);
        }
        {
            var Q0;
            Q0 = qSketchRegion(id + "F72", true);
            extrude(context, id + "F73", {"entities" : qUnion([Q0]), "operationType" : NewBodyOperationType.ADD, "depth" : 25 * mm, "offsetDistance" : 25 * mm});
        }
        {
            var Q0;
            Q0=makeQuery(id+"F73.opExtrude","CAP_FACE",FACE,{"disambiguationData":[OSD([sQuery(id+"F72.wireOp",EDGE,"E81.bottom"),sQuery(id+"F72.wireOp",EDGE,"E81.top"),sQuery(id+"F72.wireOp",EDGE,"E81.left"),sQuery(id+"F72.wireOp",EDGE,"E81.right")])],"isStart":false});
            var Q1;
            Q1=makeQuery(id+"F73.opExtrude","SWEPT_FACE",FACE,{"disambiguationData":[OSD([sQuery(id+"F72.wireOp",EDGE,"E81.top")])]});
            var Q2;
            Q2=makeQuery(id+"F73.opExtrude","SWEPT_FACE",FACE,{"disambiguationData":[OSD([sQuery(id+"F72.wireOp",EDGE,"E81.bottom")])]});
            fillet(context, id + "F74", {"entities" : qUnion([Q0, Q1, Q2]), "radius" : 12.5 * mm, "tangentPropagation" : true, "allowEdgeOverflow" : false});
        }
        {
            var Q0;
            Q0=makeQuery(id+"F73.opExtrude","CAP_FACE",FACE,{"disambiguationData":[OSD([sQuery(id+"F72.wireOp",EDGE,"E81.bottom"),sQuery(id+"F72.wireOp",EDGE,"E81.top"),sQuery(id+"F72.wireOp",EDGE,"E81.left"),sQuery(id+"F72.wireOp",EDGE,"E81.right")])],"isStart":false});
            var sketch = newSketch(context, id + "F75", { "sketchPlane" : qUnion([Q0])});
            skCircle(sketch, "E82", {"center": v(4567.73, -93.72) * mm, "radius": 38.11 * mm});
            skSolve(sketch);
        }
        {
            var Q0;
            Q0 = qSketchRegion(id + "F75", true);
            extrude(context, id + "F76", {"entities" : qUnion([Q0]), "operationType" : NewBodyOperationType.ADD, "depth" : 150 * mm, "offsetDistance" : 25 * mm});
        }
        {
            var Q0;
            Q0=makeQuery(id+"F66.boolean.opBoolean","COPY",FACE,{"derivedFrom":makeQuery(id+"F66.opExtrude","CAP_FACE",FACE,{"disambiguationData":[OSD([sQuery(id+"F65.wireOp",EDGE,"E71.bottom"),sQuery(id+"F65.wireOp",EDGE,"E71.top"),sQuery(id+"F65.wireOp",EDGE,"E71.left"),sQuery(id+"F65.wireOp",EDGE,"E71.right")])],"isStart":false})});
            var sketch = newSketch(context, id + "F77", { "sketchPlane" : qUnion([Q0])});
            skLineSegment(sketch, "E83.bottom", {"start": v(-169.04, 551.9) * mm, "end": v(124, 551.9) * mm});
            skLineSegment(sketch, "E83.top", {"start": v(-169.04, 351.2) * mm, "end": v(124, 351.2) * mm});
            skLineSegment(sketch, "E83.left", {"start": v(-169.04, 551.9) * mm, "end": v(-169.04, 351.2) * mm});
            skLineSegment(sketch, "E83.right", {"start": v(124, 551.9) * mm, "end": v(124, 351.2) * mm});
            skLineSegment(sketch, "E84.bottom", {"start": v(-146.58, 528.5) * mm, "end": v(103.08, 528.5) * mm});
            skLineSegment(sketch, "E84.top", {"start": v(-146.58, 444.78) * mm, "end": v(103.08, 444.78) * mm});
            skLineSegment(sketch, "E84.left", {"start": v(-146.58, 528.5) * mm, "end": v(-146.58, 444.78) * mm});
            skLineSegment(sketch, "E84.right", {"start": v(103.08, 528.5) * mm, "end": v(103.08, 444.78) * mm});
            skSolve(sketch);
        }
        {
            var Q0;
            Q0 = qSketchRegion(id + "F77", true);
            extrude(context, id + "F78", {"entities" : qUnion([Q0]), "operationType" : NewBodyOperationType.ADD, "depth" : 10 * mm, "offsetDistance" : 25 * mm});
        }
        {
            var Q0;
            Q0=makeQuery(id+"F60.opExtrude","CAP_FACE",FACE,{"disambiguationData":[OSD([sQuery(id+"F59.wireOp",EDGE,"E68.bottom"),sQuery(id+"F59.wireOp",EDGE,"E68.top"),sQuery(id+"F59.wireOp",EDGE,"E68.left"),sQuery(id+"F59.wireOp",EDGE,"E68.right")])],"isStart":true});
            var sketch = newSketch(context, id + "F79", { "sketchPlane" : qUnion([Q0])});
            skLineSegment(sketch, "E85.bottom", {"start": v(4227.63, 178.4) * mm, "end": v(4247.63, 178.4) * mm});
            skLineSegment(sketch, "E85.top", {"start": v(4227.63, -541.6) * mm, "end": v(4247.63, -541.6) * mm});
            skLineSegment(sketch, "E86.bottom", {"start": v(4247.63, 304.92) * mm, "end": v(4617.63, 304.92) * mm});
            skLineSegment(sketch, "E86.left", {"start": v(4247.63, 304.92) * mm, "end": v(4247.63, 178.4) * mm});
            skLineSegment(sketch, "E86.right", {"start": v(4617.63, 304.92) * mm, "end": v(4617.63, 178.4) * mm});
            skLineSegment(sketch, "E87.left", {"start": v(4247.63, -561.6) * mm, "end": v(4247.63, -541.6) * mm});
            skLineSegment(sketch, "E87.right", {"start": v(4617.63, -561.6) * mm, "end": v(4617.63, -541.6) * mm});
            skLineSegment(sketch, "E88.trimOffspring", {"start": v(4617.63, -541.6) * mm, "end": v(4637.63, -541.6) * mm});
            skLineSegment(sketch, "E89.trimOffspring", {"start": v(4617.63, 178.4) * mm, "end": v(4637.63, 178.4) * mm});
            skLineSegment(sketch, "E90.bottom", {"start": v(4227.63, 178.4) * mm, "end": v(4149.64, 178.4) * mm});
            skLineSegment(sketch, "E90.top", {"start": v(4227.63, -541.6) * mm, "end": v(4149.64, -541.6) * mm});
            skLineSegment(sketch, "E90.right", {"start": v(4149.64, 178.4) * mm, "end": v(4149.64, -541.6) * mm});
            skLineSegment(sketch, "E91.top", {"start": v(4247.63, -663.2) * mm, "end": v(4617.63, -663.2) * mm});
            skLineSegment(sketch, "E91.left", {"start": v(4247.63, -561.6) * mm, "end": v(4247.63, -663.2) * mm});
            skLineSegment(sketch, "E91.right", {"start": v(4617.63, -561.6) * mm, "end": v(4617.63, -663.2) * mm});
            skLineSegment(sketch, "E92.bottom", {"start": v(4637.63, -541.6) * mm, "end": v(4716.45, -541.6) * mm});
            skLineSegment(sketch, "E92.top", {"start": v(4637.63, 178.4) * mm, "end": v(4716.45, 178.4) * mm});
            skLineSegment(sketch, "E92.right", {"start": v(4716.45, -541.6) * mm, "end": v(4716.45, 178.4) * mm});
            skSolve(sketch);
        }
        {
            var Q0;
            Q0 = qSketchRegion(id + "F79", true);
            extrude(context, id + "F80", {"entities" : qUnion([Q0]), "operationType" : NewBodyOperationType.REMOVE, "oppositeDirection" : true, "depth" : 50 * mm, "offsetDistance" : 25 * mm, "hasDraft" : true, "draftAngle" : 20 * degree, "draftPullDirection" : true});
        }
        {
            var Q0;
            Q0=makeQuery(id+"F8.boolean.opBoolean","MERGE",FACE,{"derivedFrom":[makeQuery(id+"F2.opExtrude","CAP_FACE",FACE,{"disambiguationData":[OSD([sQuery(id+"F1.wireOp",EDGE,"E1.bottom"),sQuery(id+"F1.wireOp",EDGE,"E1.top"),sQuery(id+"F1.wireOp",EDGE,"E1.left"),sQuery(id+"F1.wireOp",EDGE,"E1.right"),sQuery(id+"F1.wireOp",EDGE,"E2.bottom"),sQuery(id+"F1.wireOp",EDGE,"E2.top"),sQuery(id+"F1.wireOp",EDGE,"E2.right"),sQuery(id+"F1.wireOp",EDGE,"E3.top"),sQuery(id+"F1.wireOp",EDGE,"E3.left"),sQuery(id+"F1.wireOp",EDGE,"E3.right")])],"isStart":false}),makeQuery(id+"F8.opExtrude","SWEPT_FACE",FACE,{"disambiguationData":[OSD([sQuery(id+"F7.wireOp",EDGE,"E6.top"),sQuery(id+"F7.wireOp",EDGE,"E7.bottom")])]})]});
            var sketch = newSketch(context, id + "F81", { "sketchPlane" : qUnion([Q0])});
            skLineSegment(sketch, "E93.bottom", {"start": v(2921.68, 3605.41) * mm, "end": v(3071.68, 3605.41) * mm});
            skLineSegment(sketch, "E93.top", {"start": v(2921.68, -1324.59) * mm, "end": v(3071.68, -1324.59) * mm});
            skLineSegment(sketch, "E93.left", {"start": v(2921.68, 3605.41) * mm, "end": v(2921.68, -1324.59) * mm});
            skLineSegment(sketch, "E93.right", {"start": v(3071.68, 3605.41) * mm, "end": v(3071.68, -1324.59) * mm});
            skSolve(sketch);
        }
        {
            var Q0;
            Q0 = qSketchRegion(id + "F81", true);
            extrude(context, id + "F82", {"entities" : qUnion([Q0]), "operationType" : NewBodyOperationType.ADD, "oppositeDirection" : true, "depth" : 250 * mm, "offsetDistance" : 25 * mm});
        }
        {
            var Q0;
            Q0=makeQuery(id+"F82.opExtrude","CAP_FACE",FACE,{"disambiguationData":[OSD([sQuery(id+"F81.wireOp",EDGE,"E93.bottom"),sQuery(id+"F81.wireOp",EDGE,"E93.top"),sQuery(id+"F81.wireOp",EDGE,"E93.left"),sQuery(id+"F81.wireOp",EDGE,"E93.right")])],"isStart":false});
            var sketch = newSketch(context, id + "F83", { "sketchPlane" : qUnion([Q0])});
            skLineSegment(sketch, "E94.bottom", {"start": v(3071.68, -1805.41) * mm, "end": v(2921.68, -1805.41) * mm});
            skLineSegment(sketch, "E94.top", {"start": v(3071.68, -1105.41) * mm, "end": v(2921.68, -1105.41) * mm});
            skLineSegment(sketch, "E94.left", {"start": v(3071.68, -1805.41) * mm, "end": v(3071.68, -1105.41) * mm});
            skLineSegment(sketch, "E94.right", {"start": v(2921.68, -1805.41) * mm, "end": v(2921.68, -1105.41) * mm});
            skSolve(sketch);
        }
        {
            var Q0;
            Q0 = qSketchRegion(id + "F83", true);
            var Q1;
            Q1=makeQuery(id+"F4.opExtrude","CAP_FACE",FACE,{"disambiguationData":[OSD([sQuery(id+"F3.wireOp",EDGE,"E4.bottom"),sQuery(id+"F3.wireOp",EDGE,"E4.top"),sQuery(id+"F3.wireOp",EDGE,"E4.left"),sQuery(id+"F3.wireOp",EDGE,"E4.right")])],"isStart":true});
            extrude(context, id + "F84", {"entities" : qUnion([Q0]), "operationType" : NewBodyOperationType.ADD, "endBound" : BoundingType.UP_TO_SURFACE, "depth" : 25 * mm, "endBoundEntityFace" : qUnion([Q1]), "offsetDistance" : 25 * mm});
        }
        {
            var Q0;
            Q0=makeQuery(id+"F84.boolean.opBoolean","MERGE",FACE,{"derivedFrom":[makeQuery(id+"F82.boolean.opBoolean","MERGE",FACE,{"derivedFrom":[makeQuery(id+"F2.opExtrude","SWEPT_FACE",FACE,{"disambiguationData":[OSD([sQuery(id+"F1.wireOp",EDGE,"E2.right"),sQuery(id+"F1.wireOp",EDGE,"E3.left")])]}),makeQuery(id+"F82.opExtrude","SWEPT_FACE",FACE,{"disambiguationData":[OSD([sQuery(id+"F81.wireOp",EDGE,"E93.right")])]})]}),makeQuery(id+"F84.opExtrude","SWEPT_FACE",FACE,{"disambiguationData":[OSD([sQuery(id+"F83.wireOp",EDGE,"E94.left")])]})]});
            var sketch = newSketch(context, id + "F85", { "sketchPlane" : qUnion([Q0])});
            skLineSegment(sketch, "E95.bottom", {"start": v(1805.41, 2250) * mm, "end": v(3605.41, 2250) * mm});
            skLineSegment(sketch, "E95.top", {"start": v(1805.41, 0) * mm, "end": v(3605.41, 0) * mm});
            skLineSegment(sketch, "E95.left", {"start": v(1805.41, 2250) * mm, "end": v(1805.41, 0) * mm});
            skLineSegment(sketch, "E95.right", {"start": v(3605.41, 2250) * mm, "end": v(3605.41, 0) * mm});
            skLineSegment(sketch, "E96.0", {"start": v(1855.41, 2200) * mm, "end": v(3555.41, 2200) * mm});
            skLineSegment(sketch, "E96.1", {"start": v(1855.41, 2200) * mm, "end": v(1855.41, 50) * mm});
            skLineSegment(sketch, "E96.2", {"start": v(1855.41, 50) * mm, "end": v(3555.41, 50) * mm});
            skLineSegment(sketch, "E96.3", {"start": v(3555.41, 2200) * mm, "end": v(3555.41, 50) * mm});
            skSolve(sketch);
        }
        {
            var Q0;
            Q0 = qSketchRegion(id + "F85", true);
            extrude(context, id + "F86", {"entities" : qUnion([Q0]), "oppositeDirection" : true, "depth" : 100 * mm, "offsetDistance" : 25 * mm, "hasSecondDirection" : true, "secondDirectionOppositeDirection" : true, "secondDirectionDepth" : 50 * mm});
        }
    });
